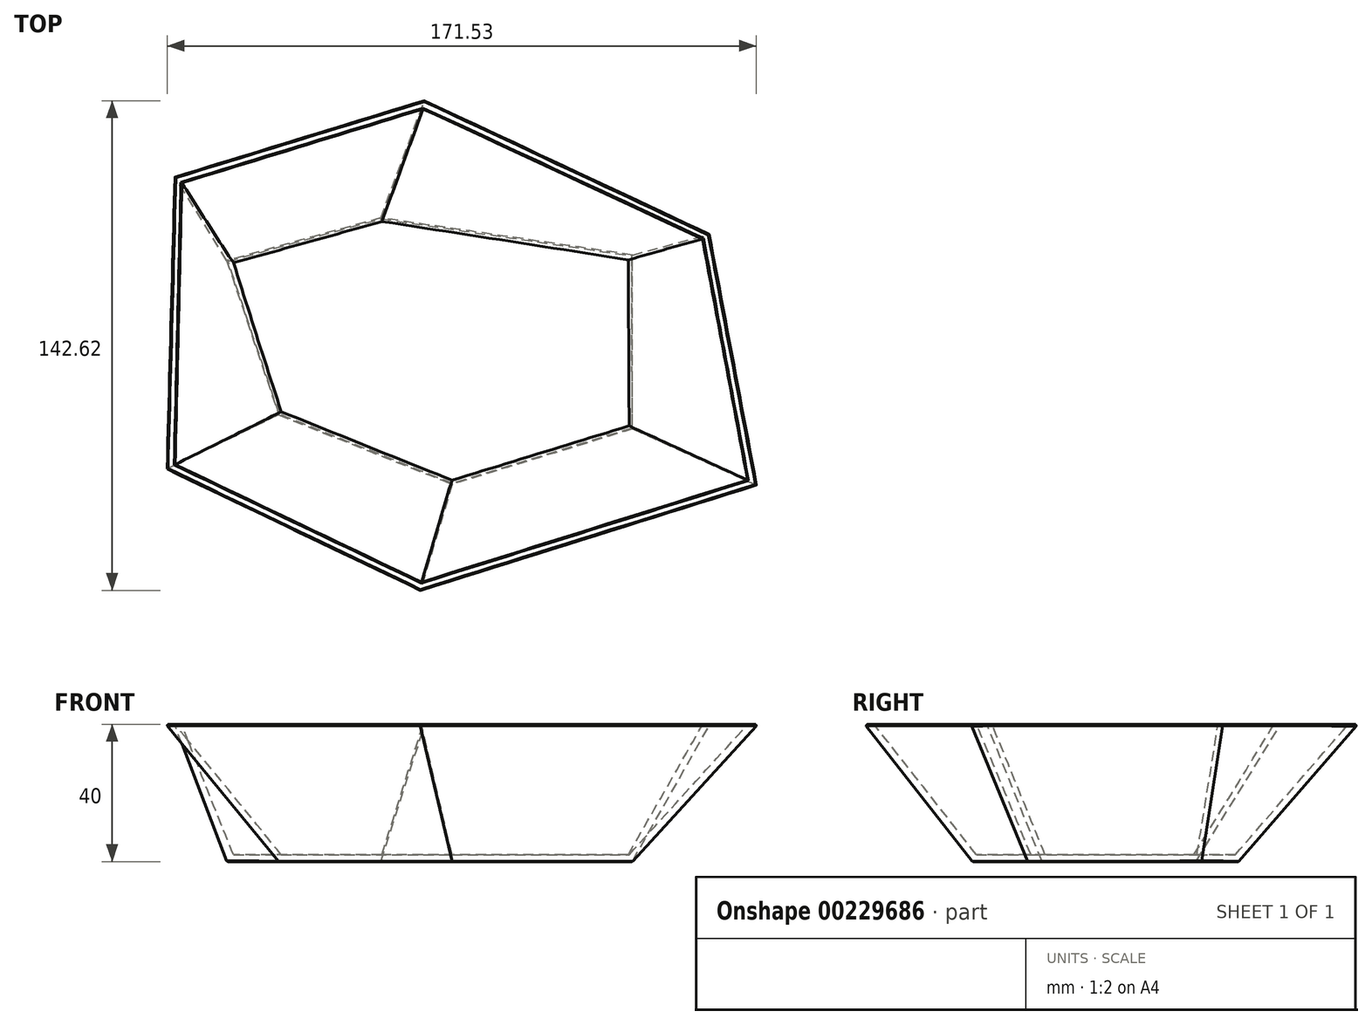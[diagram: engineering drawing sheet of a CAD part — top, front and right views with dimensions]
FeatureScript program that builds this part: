
annotation { "Feature Type Name" : "Feature", "Feature Type Description" : "" }
export const myFeature = defineFeature(function(context is Context, id is Id, definition is map)
    precondition{}
    {
        {
            var Q0;
            Q0=qCreatedBy(makeId("Top.planeOp"),FACE);
            var sketch = newSketch(context, id + "F0", { "sketchPlane" : qUnion([Q0])});
            skLineSegment(sketch, "E0", {"start": v(-31.22, -25.55) * mm, "end": v(19.23, -45.73) * mm});
            skLineSegment(sketch, "E1", {"start": v(19.23, -45.73) * mm, "end": v(71.58, -29.65) * mm});
            skLineSegment(sketch, "E2", {"start": v(71.58, -29.65) * mm, "end": v(71.58, 20.91) * mm});
            skLineSegment(sketch, "E3", {"start": v(71.58, 20.91) * mm, "end": v(-1.6, 31.66) * mm});
            skLineSegment(sketch, "E4", {"start": v(-1.6, 31.66) * mm, "end": v(-46.36, 19.22) * mm});
            skLineSegment(sketch, "E5", {"start": v(-46.36, 19.22) * mm, "end": v(-31.22, -25.55) * mm});
            skSolve(sketch);
        }
        {
            var Q0;
            Q0=qCreatedBy(makeId("Top.planeOp"),FACE);
            cPlane(context, id + "F1", {"entities" : qUnion([Q0]), "cplaneType" : CPlaneType.OFFSET, "offset" : 40 * mm, "width" : 150 * mm, "height" : 150 * mm});
        }
        {
            var Q0;
            Q0=qCreatedBy(id+"F1.planeOp",FACE);
            var sketch = newSketch(context, id + "F2", { "sketchPlane" : qUnion([Q0])});
            skLineSegment(sketch, "E6", {"start": v(11.26, 66.33) * mm, "end": v(94.23, 27.03) * mm});
            skLineSegment(sketch, "E7", {"start": v(94.23, 27.03) * mm, "end": v(108.18, -46.26) * mm});
            skLineSegment(sketch, "E8", {"start": v(108.18, -46.26) * mm, "end": v(9.8, -77.1) * mm});
            skLineSegment(sketch, "E9", {"start": v(9.8, -77.1) * mm, "end": v(-64.2, -41.58) * mm});
            skLineSegment(sketch, "E10", {"start": v(-64.2, -41.58) * mm, "end": v(-61.67, 43.93) * mm});
            skLineSegment(sketch, "E11", {"start": v(-61.67, 43.93) * mm, "end": v(11.26, 66.33) * mm});
            skSolve(sketch);
        }
        {
            var Q0;
            Q0 = qSketchRegion(id + "F0", true);
            var Q1;
            Q1 = qSketchRegion(id + "F2", true);
            var Q2;
            Q2=sQuery(id+"F2.wireOp",VERTEX,"E10.start");
            var Q3;
            Q3=sQuery(id+"F0.wireOp",VERTEX,"E5.start");
            loft(context, id + "F3", {"sheetProfilesArray" : [{ "sheetProfileEntities" : qUnion([Q0]) }, { "sheetProfileEntities" : qUnion([Q1]) }], "connections" : [{ "connectionEntities" : qUnion([Q2, Q3]), "connectionEdgeQueries" : qUnion([]), "connectionEdgeParameters" : [] }]});
        }
        {
            var Q0;
            Q0=makeQuery(id+"F3.opLoft","CAP_FACE",FACE,{"disambiguationData":[OSD([makeQuery(id+"F2.imprint","IMPRINT",FACE,{"disambiguationData":[TD([[makeQuery(id+"F2.imprint","IMPRINT",EDGE,{"derivedFrom":sQuery(id+"F2.wireOp",EDGE,"E6")}),-1.0]])]})])],"isStart":true});
            shell(context, id + "F4", {"entities" : qUnion([Q0]), "thickness" : 2 * mm});
        }
        {
            var Q0;
            Q0=makeQuery(id+"F3.opLoft","CAP_FACE",FACE,{"disambiguationData":[OSD([makeQuery(id+"F0.imprint","IMPRINT",FACE,{"disambiguationData":[TD([[makeQuery(id+"F0.imprint","IMPRINT",EDGE,{"derivedFrom":sQuery(id+"F0.wireOp",EDGE,"E0")}),1.0]])]})])],"isStart":true});
            var Q1;
            Q1=makeQuery(id+"F3.opLoft","CAP_FACE",FACE,{"disambiguationData":[OSD([makeQuery(id+"F2.imprint","IMPRINT",FACE,{"disambiguationData":[TD([[makeQuery(id+"F2.imprint","IMPRINT",EDGE,{"derivedFrom":sQuery(id+"F2.wireOp",EDGE,"E6")}),-1.0]])]})])],"isStart":true});
            chamfer(context, id + "F5", {"entities" : qUnion([Q0, Q1]), "width" : 0.3 * mm, "tangentPropagation" : true});
        }
    });
